# Revit family: QF_ELECTROLUXPROFESSIONAL_1LSNA4_TE1220G_G
name_source: partatom
category: Attrezzature speciali
units: mm (PartAtom-declared; Revit-internal decimal feet)

## family parameters
Basato su piano di lavoro = No
Condiviso = No
Punto di calcolo locali = No
Quota connettore circolare = Usa diametro
Sempre verticale = Sì
Taglio con vuoti quando caricato = No
Tipo di parte = Normale

## types (2) — shared parameters
Depth = 822 mm
Depth Actual = 822 mm
Gas KW = 6
Height = 850 mm
Height Actual = 1098 mm  [stored 3.60236 ft]
Latent Heat Output = 0.0
Length Actual = 686 mm  [stored 2.25066 ft]
Modello = TE1220G
Phase = 1
Produttore = Electrolux Professional
Sensible Heat Output = 0.0
URL = www.electroluxprofessional.com
Volts = 240 V
Watts = 11000 W
Weight = 78
Width = 686 mm  [stored 2.25066 ft]
zero-valued in all types: Prospetto di default, Steam Pounds per Hour

## per-type parameters (varying)
| type | Cycle | Descrizione | Item Number |
| 988690054 | 50 Hz | myPRO XL SMART PROFESSIONAL TUMBLE DRYER TE1220G 12KG GAS 5,7KW VENTED 220-240/50/1N 1,1KW SYMBOLS SST/DARK BLUE | 1L0GJY |
| 988690056 | 60 Hz | myPRO XL SMART PROFESSIONAL TUMBLE DRYER TE1220G GAS 5,7KW VENTED 208-240/60/1 1,1KW SYMBOLS SST/DARK BLUE | 1L0H4K |

note: [stored X ft] marks values corroborated as IEEE doubles in the binary element streams (Revit-internal decimal feet)

## geometry (parser evidence)
native form markers: Sweep x2
no freeform markers — native parametric forms only
